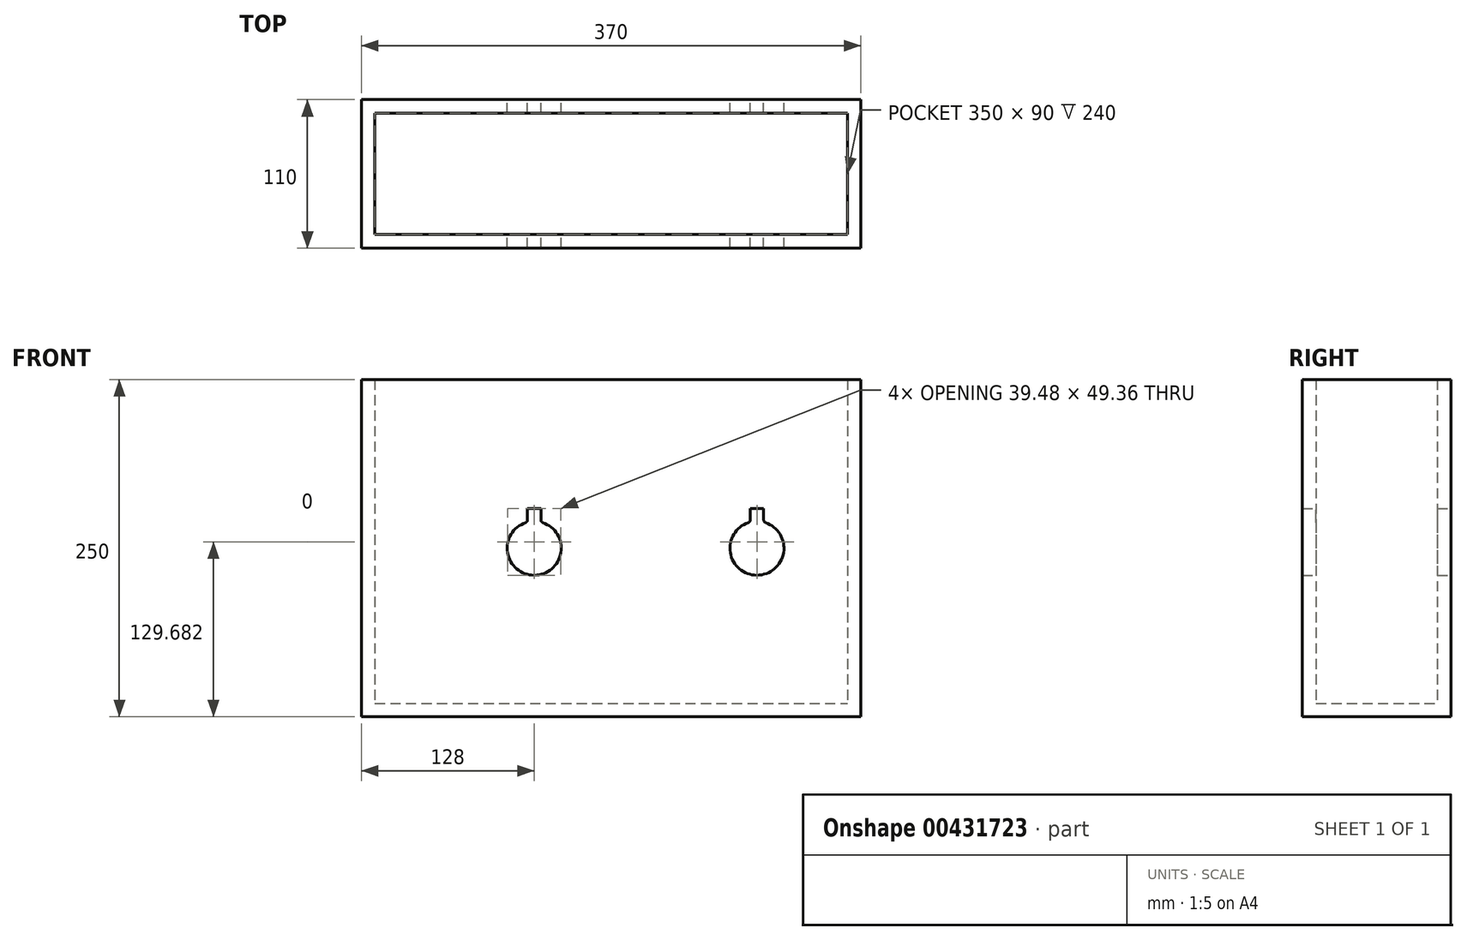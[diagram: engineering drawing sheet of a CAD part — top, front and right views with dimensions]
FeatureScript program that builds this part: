
annotation { "Feature Type Name" : "Feature", "Feature Type Description" : "" }
export const myFeature = defineFeature(function(context is Context, id is Id, definition is map)
    precondition{}
    {
        {
            var Q0;
            Q0=qCreatedBy(makeId("Front.planeOp"),FACE);
            var sketch = newSketch(context, id + "F0", { "sketchPlane" : qUnion([Q0])});
            skLineSegment(sketch, "E0.bottom", {"start": v(-243, 125) * mm, "end": v(127, 125) * mm});
            skLineSegment(sketch, "E0.top", {"start": v(-243, -125) * mm, "end": v(127, -125) * mm});
            skLineSegment(sketch, "E0.left", {"start": v(-243, 125) * mm, "end": v(-243, -125) * mm});
            skLineSegment(sketch, "E0.right", {"start": v(127, 125) * mm, "end": v(127, -125) * mm});
            skPoint(sketch, "E1", {"position": v(-58, 125) * mm});
            skPoint(sketch, "E2", {"position": v(127, 0) * mm});
            skArc(sketch, "E3", {"start": v(-121.36, 18.96) * mm, "mid": v(-115, -20) * mm, "end": v(-108.64, 18.96) * mm});
            skArc(sketch, "E4", {"start": v(43.64, 18.96) * mm, "mid": v(50, -20) * mm, "end": v(56.36, 18.96) * mm});
            skLineSegment(sketch, "E5", {"start": v(-115, 40.67) * mm, "end": v(-115, 0) * mm, "construction": true});
            skLineSegment(sketch, "E6", {"start": v(-120, 20.86) * mm, "end": v(-120, 29.36) * mm});
            skLineSegment(sketch, "E7", {"start": v(-120, 29.36) * mm, "end": v(-110, 29.36) * mm});
            skLineSegment(sketch, "E8", {"start": v(-110, 29.36) * mm, "end": v(-110, 20.86) * mm});
            skPoint(sketch, "E9", {"position": v(-115, 29.36) * mm});
            skLineSegment(sketch, "E10", {"start": v(50, 0) * mm, "end": v(50, 20.74) * mm, "construction": true});
            skLineSegment(sketch, "E11", {"start": v(45, 20.86) * mm, "end": v(45, 29.36) * mm});
            skLineSegment(sketch, "E12", {"start": v(45, 29.36) * mm, "end": v(55, 29.36) * mm});
            skLineSegment(sketch, "E13", {"start": v(55, 29.36) * mm, "end": v(55, 20.86) * mm});
            skPoint(sketch, "E14", {"position": v(50, 29.36) * mm});
            skPoint(sketch, "E15.visualSharp", {"position": v(-120, 19.36) * mm});
            skArc(sketch, "E15.filletArc", {"start": v(-121.36, 18.96) * mm, "mid": v(-120.38, 19.69) * mm, "end": v(-120, 20.86) * mm});
            skPoint(sketch, "E16.visualSharp", {"position": v(-110, 19.36) * mm});
            skArc(sketch, "E16.filletArc", {"start": v(-110, 20.86) * mm, "mid": v(-109.62, 19.69) * mm, "end": v(-108.64, 18.96) * mm});
            skPoint(sketch, "E17.visualSharp", {"position": v(45, 19.36) * mm});
            skArc(sketch, "E17.filletArc", {"start": v(43.64, 18.96) * mm, "mid": v(44.62, 19.69) * mm, "end": v(45, 20.86) * mm});
            skPoint(sketch, "E18.visualSharp", {"position": v(55, 19.36) * mm});
            skArc(sketch, "E18.filletArc", {"start": v(55, 20.86) * mm, "mid": v(55.38, 19.69) * mm, "end": v(56.36, 18.96) * mm});
            skSolve(sketch);
        }
        {
            var Q0;
            Q0 = qSketchRegion(id + "F0", true);
            extrude(context, id + "F1", {"entities" : qUnion([Q0]), "endBound" : BoundingType.SYMMETRIC, "depth" : 110 * mm});
        }
        {
            var Q0;
            Q0=makeQuery(id+"F1.opExtrude","SWEPT_FACE",FACE,{"disambiguationData":[OSD([sQuery(id+"F0.wireOp",EDGE,"E0.bottom")])]});
            var Q1;
            Q1=makeQuery(id+"F1.opExtrude","SWEPT_FACE",FACE,{"disambiguationData":[OSD([sQuery(id+"F0.wireOp",EDGE,"E3")])]});
            var Q2;
            Q2=makeQuery(id+"F1.opExtrude","SWEPT_FACE",FACE,{"disambiguationData":[OSD([sQuery(id+"F0.wireOp",EDGE,"E15.filletArc")])]});
            var Q3;
            Q3=makeQuery(id+"F1.opExtrude","SWEPT_FACE",FACE,{"disambiguationData":[OSD([sQuery(id+"F0.wireOp",EDGE,"E6")])]});
            var Q4;
            Q4=makeQuery(id+"F1.opExtrude","SWEPT_FACE",FACE,{"disambiguationData":[OSD([sQuery(id+"F0.wireOp",EDGE,"E7")])]});
            var Q5;
            Q5=makeQuery(id+"F1.opExtrude","SWEPT_FACE",FACE,{"disambiguationData":[OSD([sQuery(id+"F0.wireOp",EDGE,"E8")])]});
            var Q6;
            Q6=makeQuery(id+"F1.opExtrude","SWEPT_FACE",FACE,{"disambiguationData":[OSD([sQuery(id+"F0.wireOp",EDGE,"E16.filletArc")])]});
            var Q7;
            Q7=makeQuery(id+"F1.opExtrude","SWEPT_FACE",FACE,{"disambiguationData":[OSD([sQuery(id+"F0.wireOp",EDGE,"E4")])]});
            var Q8;
            Q8=makeQuery(id+"F1.opExtrude","SWEPT_FACE",FACE,{"disambiguationData":[OSD([sQuery(id+"F0.wireOp",EDGE,"E18.filletArc")])]});
            var Q9;
            Q9=makeQuery(id+"F1.opExtrude","SWEPT_FACE",FACE,{"disambiguationData":[OSD([sQuery(id+"F0.wireOp",EDGE,"E13")])]});
            var Q10;
            Q10=makeQuery(id+"F1.opExtrude","SWEPT_FACE",FACE,{"disambiguationData":[OSD([sQuery(id+"F0.wireOp",EDGE,"E12")])]});
            var Q11;
            Q11=makeQuery(id+"F1.opExtrude","SWEPT_FACE",FACE,{"disambiguationData":[OSD([sQuery(id+"F0.wireOp",EDGE,"E11")])]});
            var Q12;
            Q12=makeQuery(id+"F1.opExtrude","SWEPT_FACE",FACE,{"disambiguationData":[OSD([sQuery(id+"F0.wireOp",EDGE,"E17.filletArc")])]});
            shell(context, id + "F2", {"entities" : qUnion([Q0, Q1, Q2, Q3, Q4, Q5, Q6, Q7, Q8, Q9, Q10, Q11, Q12]), "thickness" : 10 * mm});
        }
    });
